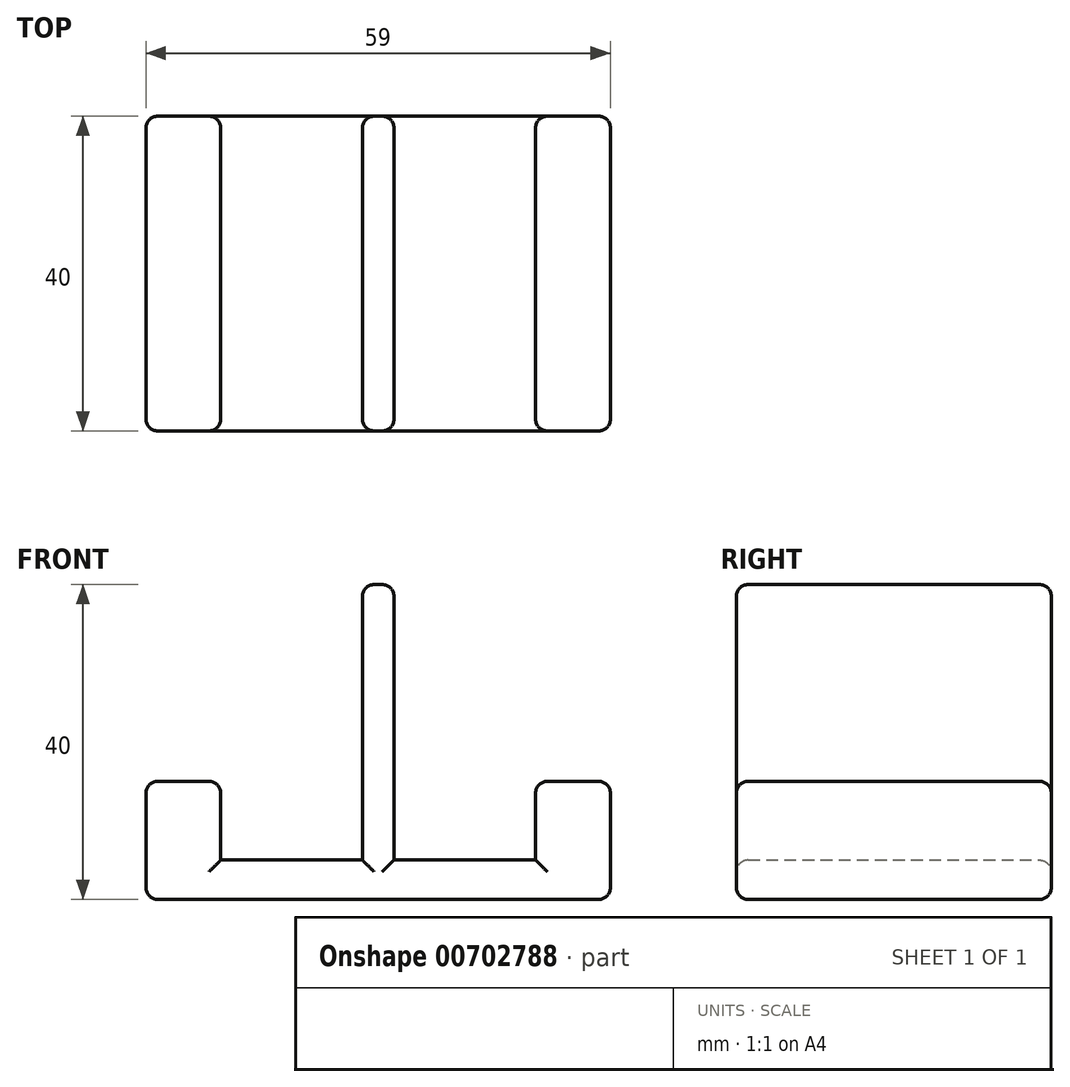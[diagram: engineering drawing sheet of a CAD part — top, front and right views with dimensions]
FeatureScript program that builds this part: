
annotation { "Feature Type Name" : "Feature", "Feature Type Description" : "" }
export const myFeature = defineFeature(function(context is Context, id is Id, definition is map)
    precondition{}
    {
        {
            var Q0;
            Q0=qCreatedBy(makeId("Front.planeOp"),FACE);
            var sketch = newSketch(context, id + "F0", { "sketchPlane" : qUnion([Q0])});
            skLineSegment(sketch, "E0", {"start": v(-29.5, 15) * mm, "end": v(-29.5, 0) * mm});
            skLineSegment(sketch, "E1", {"start": v(-29.5, 0) * mm, "end": v(29.5, 0) * mm});
            skLineSegment(sketch, "E2", {"start": v(29.5, 0) * mm, "end": v(29.5, 15) * mm});
            skLineSegment(sketch, "E3", {"start": v(29.5, 15) * mm, "end": v(20, 15) * mm});
            skLineSegment(sketch, "E4", {"start": v(20, 15) * mm, "end": v(20, 5) * mm});
            skLineSegment(sketch, "E5", {"start": v(20, 5) * mm, "end": v(2, 5) * mm});
            skLineSegment(sketch, "E6", {"start": v(2, 5) * mm, "end": v(2, 40) * mm});
            skLineSegment(sketch, "E7", {"start": v(2, 40) * mm, "end": v(-2, 40) * mm});
            skLineSegment(sketch, "E8", {"start": v(-2, 40) * mm, "end": v(-2, 5) * mm});
            skLineSegment(sketch, "E9", {"start": v(-2, 5) * mm, "end": v(-20, 5) * mm});
            skLineSegment(sketch, "E10", {"start": v(-20, 5) * mm, "end": v(-20, 15) * mm});
            skLineSegment(sketch, "E11", {"start": v(-20, 15) * mm, "end": v(-29.5, 15) * mm});
            skSolve(sketch);
        }
        {
            var Q0;
            Q0 = qSketchRegion(id + "F0", true);
            extrude(context, id + "F1", {"entities" : qUnion([Q0]), "depth" : 40 * mm, "offsetDistance" : 25 * mm});
        }
        {
            var Q0;
            Q0=makeQuery(id+"F1.opExtrude","CAP_FACE",FACE,{"disambiguationData":[OSD([sQuery(id+"F0.wireOp",EDGE,"E0"),sQuery(id+"F0.wireOp",EDGE,"E1"),sQuery(id+"F0.wireOp",EDGE,"E2"),sQuery(id+"F0.wireOp",EDGE,"E3"),sQuery(id+"F0.wireOp",EDGE,"E4"),sQuery(id+"F0.wireOp",EDGE,"E5"),sQuery(id+"F0.wireOp",EDGE,"E6"),sQuery(id+"F0.wireOp",EDGE,"E7"),sQuery(id+"F0.wireOp",EDGE,"E8"),sQuery(id+"F0.wireOp",EDGE,"E9"),sQuery(id+"F0.wireOp",EDGE,"E10"),sQuery(id+"F0.wireOp",EDGE,"E11")])],"isStart":false});
            var Q1;
            Q1=makeQuery(id+"F1.opExtrude","SWEPT_FACE",FACE,{"disambiguationData":[OSD([sQuery(id+"F0.wireOp",EDGE,"E3")])]});
            var Q2;
            Q2=makeQuery(id+"F1.opExtrude","SWEPT_FACE",FACE,{"disambiguationData":[OSD([sQuery(id+"F0.wireOp",EDGE,"E7")])]});
            var Q3;
            Q3=makeQuery(id+"F1.opExtrude","SWEPT_FACE",FACE,{"disambiguationData":[OSD([sQuery(id+"F0.wireOp",EDGE,"E11")])]});
            var Q4;
            Q4=makeQuery(id+"F1.opExtrude","CAP_FACE",FACE,{"disambiguationData":[OSD([sQuery(id+"F0.wireOp",EDGE,"E0"),sQuery(id+"F0.wireOp",EDGE,"E1"),sQuery(id+"F0.wireOp",EDGE,"E2"),sQuery(id+"F0.wireOp",EDGE,"E3"),sQuery(id+"F0.wireOp",EDGE,"E4"),sQuery(id+"F0.wireOp",EDGE,"E5"),sQuery(id+"F0.wireOp",EDGE,"E6"),sQuery(id+"F0.wireOp",EDGE,"E7"),sQuery(id+"F0.wireOp",EDGE,"E8"),sQuery(id+"F0.wireOp",EDGE,"E9"),sQuery(id+"F0.wireOp",EDGE,"E10"),sQuery(id+"F0.wireOp",EDGE,"E11")])],"isStart":true});
            var Q5;
            Q5=makeQuery(id+"F1.opExtrude","SWEPT_EDGE",EDGE,{"disambiguationData":[OSD([sQuery(id+"F0.wireOp",EDGE,"E1"),sQuery(id+"F0.wireOp",EDGE,"E2")])]});
            var Q6;
            Q6=makeQuery(id+"F1.opExtrude","SWEPT_EDGE",EDGE,{"disambiguationData":[OSD([sQuery(id+"F0.wireOp",EDGE,"E0"),sQuery(id+"F0.wireOp",EDGE,"E1")])]});
            fillet(context, id + "F2", {"entities" : qUnion([Q0, Q1, Q2, Q3, Q4, Q5, Q6]), "radius" : 1.5 * mm, "tangentPropagation" : true, "allowEdgeOverflow" : false});
        }
    });
